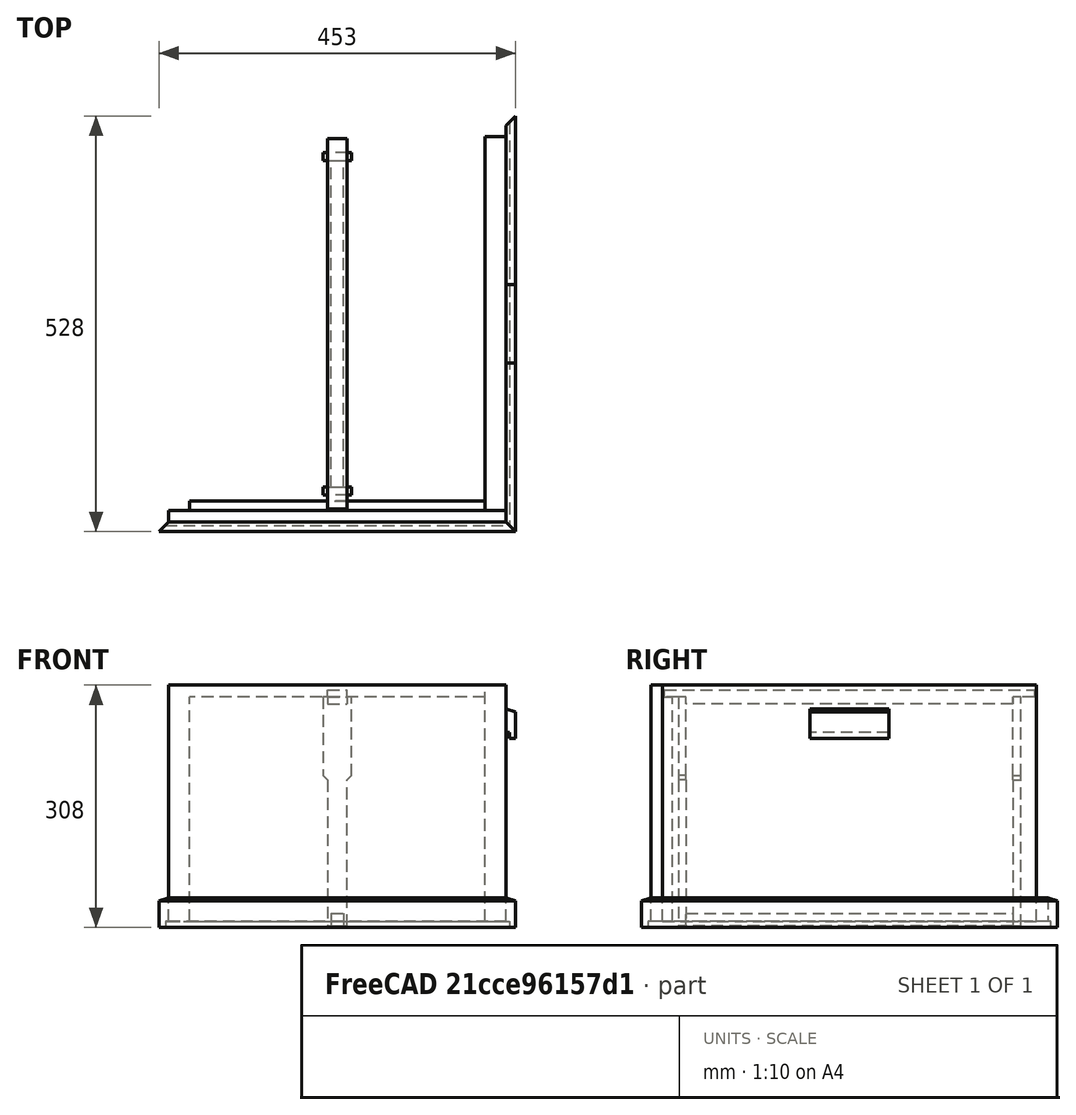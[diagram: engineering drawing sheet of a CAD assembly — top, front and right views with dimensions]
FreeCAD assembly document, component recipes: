
FREECAD ASSEMBLY — COMPONENT RECIPES ("naklada")

This assembly document has 6 components, labeled P0..P5 below (a component is one placed body or linked part). 6 of them carry a construction recipe — the FreeCAD feature program that regenerates the part from scratch, quoted from this document or its linked companion documents; the rest are supplied as boundary geometry only. No exploded tour is included for this assembly.
COMPONENT P0 — recipe-attached ("slat_side", modeled in this document).
Construction recipe (the document's own serialized feature program — sketch geometry with constraints, then the solid features built on it; lengths are millimeters unless a unit is written):

FEATURE [PartDesign::CoordinateSystem] LCS_0005
  AttacherType = Attacher::AttachEngine3D
  MapMode = 2
  Support = -> [X_Axis006]
FEATURE [Sketcher::SketchObject] Sketch003  label="Sketch004"
  FullyConstrained = true
  MapMode = 5
  Placement = pos=(0,0,0) rot=(1,0,0;1.5708rad)
  Support = -> [XZ_Plane006]
  expr: Constraints[12] = Variables.inner_width / 2 + Variables.wall_thickness
  sketch-geometry (6):
    g0: LineSegment StartX=214.5 StartY=0 StartZ=0 EndX=218.5 EndY=0 EndZ=0
    g1: LineSegment StartX=218.5 StartY=0 StartZ=0 EndX=218.5 EndY=-8 EndZ=0
    g2: LineSegment StartX=218.5 StartY=-8 StartZ=0 EndX=226.5 EndY=-8 EndZ=0
    g3: LineSegment StartX=226.5 StartY=-8 StartZ=0 EndX=226.5 EndY=25.6324 EndZ=0
    g4: LineSegment StartX=214.5 StartY=30 StartZ=0 EndX=214.5 EndY=0 EndZ=0
    g5: LineSegment StartX=214.5 StartY=30 StartZ=0 EndX=226.5 EndY=25.6324 EndZ=0
  constraints (18):
    c: Horizontal(g0)
    c: Coincident(g0,g1)
    c: Vertical(g1)
    c: Coincident(g1,g2)
    c: Horizontal(g2)
    c: Coincident(g2,g3)
    c: Vertical(g3)
    c: Coincident(g4,g0)
    c: Vertical(g4)
    c: DistanceX(g0,g0) = 4  'c'
    c: DistanceY(g1,g1) = 8  'd'
    c: Horizontal(g0,g-1)
    c: DistanceX(g-1,g0) = 214.5
    c: DistanceX(g0,g2) = 12  'a'
    c: DistanceY(g4,g4) = 30  'b'
    c: Coincident(g5,g4)
    c: Coincident(g5,g3)
    c: Angle(g5) = -0.349066  'e'
FEATURE [PartDesign::Pad] Pad002
  Direction = (1,1,1)
  Length = 700
  Length2 = 100
  Midplane = true
  Placement = pos=(0,0,0) rot=(1,0,0;1.5708rad)
  Profile = -> Sketch003
  Type = 0
FEATURE [Sketcher::SketchObject] Sketch004  label="Sketch005"
  ExternalGeometry = -> [Pad002]
  FullyConstrained = true
  MapMode = 5
  Support = -> [XY_Plane006]
  expr: Constraints[14] = Variables.inner_depth + 2 * Variables.wall_thickness
  sketch-geometry (8):
    g0: LineSegment StartX=226.5 StartY=-350 StartZ=0 EndX=226.5 EndY=-264 EndZ=0
    g1: LineSegment StartX=226.5 StartY=-264 StartZ=0 EndX=214.5 EndY=-252 EndZ=0
    g2: LineSegment StartX=214.5 StartY=-252 StartZ=0 EndX=214.5 EndY=-350 EndZ=0
    g3: LineSegment StartX=226.5 StartY=350 StartZ=0 EndX=226.5 EndY=264 EndZ=0
    g4: LineSegment StartX=226.5 StartY=264 StartZ=0 EndX=214.5 EndY=252 EndZ=0
    g5: LineSegment StartX=214.5 StartY=252 StartZ=0 EndX=214.5 EndY=350 EndZ=0
    g6: LineSegment StartX=214.5 StartY=-350 StartZ=0 EndX=226.5 EndY=-350 EndZ=0
    g7: LineSegment StartX=214.5 StartY=350 StartZ=0 EndX=226.5 EndY=350 EndZ=0
  constraints (20):
    c: Coincident(g0,g-4)
    c: Coincident(g1,g0)
    c: Coincident(g2,g1)
    c: Coincident(g2,g-4)
    c: Vertical(g2)
    c: Vertical(g0)
    c: Coincident(g-3,g3)
    c: Vertical(g3)
    c: Coincident(g3,g4)
    c: Coincident(g4,g5)
    c: Coincident(g5,g-3)
    c: Vertical(g5)
    c: Equal(g4,g1)
    c: Equal(g5,g2)
    c: DistanceY(g1,g4) = 504
    c: Coincident(g6,g2)
    c: Coincident(g6,g0)
    c: Coincident(g7,g5)
    c: Coincident(g7,g3)
    c: Perpendicular(g4,g1)
FEATURE [PartDesign::Pocket] Pocket001
  BaseFeature = -> Pad002
  Length = 41
  Length2 = 100
  Midplane = true
  Placement = pos=(0,0,0) rot=(1,0,0;1.5708rad)
  Profile = -> Sketch004
  Type = 1
FEATURE [PartDesign::Body] Body_3
  Group = -> [LCS_0005,Sketch003,Pad002,Sketch004,Pocket001]
  Origin = -> Origin006
  Tip = -> Pocket001
COMPONENT P1 — recipe-attached ("slat_front_rear", modeled in this document).
Construction recipe (the document's own serialized feature program — sketch geometry with constraints, then the solid features built on it; lengths are millimeters unless a unit is written):

FEATURE [PartDesign::CoordinateSystem] LCS_0007
  AttacherType = Attacher::AttachEngine3D
  MapMode = 2
  Support = -> [X_Axis008]
FEATURE [Sketcher::SketchObject] Sketch005  label="Sketch006"
  FullyConstrained = true
  MapMode = 5
  Placement = pos=(0,0,0) rot=(0.57735,0.57735,0.57735;2.0944rad)
  Support = -> [YZ_Plane008]
  expr: Constraints[17] = Variables.inner_depth / 2 + Variables.wall_thickness
  sketch-geometry (6):
    g0: LineSegment StartX=-252 StartY=0 StartZ=0 EndX=-252 EndY=30 EndZ=0
    g1: LineSegment StartX=-264 StartY=25.6324 StartZ=0 EndX=-264 EndY=-8 EndZ=0
    g2: LineSegment StartX=-264 StartY=-8 StartZ=0 EndX=-256 EndY=-8 EndZ=0
    g3: LineSegment StartX=-256 StartY=-8 StartZ=0 EndX=-256 EndY=0 EndZ=0
    g4: LineSegment StartX=-256 StartY=0 StartZ=0 EndX=-252 EndY=0 EndZ=0
    g5: LineSegment StartX=-264 StartY=25.6324 StartZ=0 EndX=-252 EndY=30 EndZ=0
  constraints (18):
    c: Vertical(g0)
    c: Vertical(g1)
    c: Coincident(g1,g2)
    c: Horizontal(g2)
    c: Coincident(g2,g3)
    c: Vertical(g3)
    c: Coincident(g3,g4)
    c: Coincident(g4,g0)
    c: Horizontal(g4)
    c: Horizontal(g0,g-1)
    c: DistanceX(g4,g4) = 4
    c: DistanceY(g3,g3) = 8
    c: DistanceX(g1,g0) = 12
    c: DistanceY(g0,g0) = 30
    c: Coincident(g5,g1)
    c: Coincident(g5,g0)
    c: Angle(g5) = 0.349066
    c: DistanceX(g0,g-1) = 252
FEATURE [PartDesign::Pad] Pad003
  Direction = (1,1,1)
  Length = 700
  Length2 = 100
  Midplane = true
  Placement = pos=(0,0,0) rot=(0.57735,0.57735,0.57735;2.0944rad)
  Profile = -> Sketch005
  Type = 0
FEATURE [Sketcher::SketchObject] Sketch006  label="Sketch007"
  ExternalGeometry = -> [Pad003]
  FullyConstrained = true
  MapMode = 5
  Support = -> [XY_Plane008]
  expr: Constraints[19] = Variables.inner_width + 2 * Variables.wall_thickness
  sketch-geometry (8):
    g0: LineSegment StartX=-350 StartY=-264 StartZ=0 EndX=-350 EndY=-252 EndZ=0
    g1: LineSegment StartX=-350 StartY=-252 StartZ=0 EndX=-214.5 EndY=-252 EndZ=0
    g2: LineSegment StartX=-214.5 StartY=-252 StartZ=0 EndX=-226.5 EndY=-264 EndZ=0
    g3: LineSegment StartX=-226.5 StartY=-264 StartZ=0 EndX=-350 EndY=-264 EndZ=0
    g4: LineSegment StartX=350 StartY=-264 StartZ=0 EndX=350 EndY=-252 EndZ=0
    g5: LineSegment StartX=350 StartY=-252 StartZ=0 EndX=214.5 EndY=-252 EndZ=0
    g6: LineSegment StartX=214.5 StartY=-252 StartZ=0 EndX=226.5 EndY=-264 EndZ=0
    g7: LineSegment StartX=226.5 StartY=-264 StartZ=0 EndX=350 EndY=-264 EndZ=0
  constraints (20):
    c: Coincident(g-3,g0)
    c: Coincident(g0,g-3)
    c: Coincident(g0,g1)
    c: Coincident(g1,g2)
    c: Coincident(g2,g3)
    c: Coincident(g3,g0)
    c: Coincident(g-4,g4)
    c: Coincident(g4,g-4)
    c: Coincident(g4,g5)
    c: Coincident(g5,g6)
    c: Coincident(g6,g7)
    c: Coincident(g7,g4)
    c: Perpendicular(g2,g6)
    c: Equal(g2,g6)
    c: Equal(g1,g5)
    c: Horizontal(g1)
    c: Horizontal(g3)
    c: Horizontal(g7)
    c: Horizontal(g5)
    c: DistanceX(g1,g5) = 429
FEATURE [PartDesign::Pocket] Pocket002
  BaseFeature = -> Pad003
  Length = 5
  Length2 = 100
  Midplane = true
  Placement = pos=(0,0,0) rot=(0.57735,0.57735,0.57735;2.0944rad)
  Profile = -> Sketch006
  Type = 1
FEATURE [PartDesign::Body] Body_4
  Group = -> [LCS_0007,Sketch005,Pad003,Sketch006,Pocket002]
  Origin = -> Origin008
  Tip = -> Pocket002
COMPONENT P2 — recipe-attached ("handle", modeled in this document).
Construction recipe (the document's own serialized feature program — sketch geometry with constraints, then the solid features built on it; lengths are millimeters unless a unit is written):

FEATURE [Sketcher::SketchObject] Sketch007  label="Sketch008"
  FullyConstrained = true
  MapMode = 5
  Placement = pos=(0,0,0) rot=(1,0,0;1.5708rad)
  Support = -> [XZ_Plane009]
  expr: Constraints[11] = Variables.inner_width / 2 + Variables.wall_thickness
  expr: Constraints[17] = Variables.height - 30
  sketch-geometry (6):
    g0: LineSegment StartX=214.5 StartY=240 StartZ=0 EndX=218.5 EndY=240 EndZ=0
    g1: LineSegment StartX=218.5 StartY=240 StartZ=0 EndX=218.5 EndY=232 EndZ=0
    g2: LineSegment StartX=218.5 StartY=232 StartZ=0 EndX=226.5 EndY=232 EndZ=0
    g3: LineSegment StartX=226.5 StartY=232 StartZ=0 EndX=226.5 EndY=265.632 EndZ=0
    g4: LineSegment StartX=214.5 StartY=270 StartZ=0 EndX=214.5 EndY=240 EndZ=0
    g5: LineSegment StartX=214.5 StartY=270 StartZ=0 EndX=226.5 EndY=265.632 EndZ=0
  constraints (18):
    c: Horizontal(g0)
    c: Coincident(g0,g1)
    c: Vertical(g1)
    c: Coincident(g1,g2)
    c: Horizontal(g2)
    c: Coincident(g2,g3)
    c: Vertical(g3)
    c: Coincident(g4,g0)
    c: Vertical(g4)
    c: DistanceX(g0,g0) = 4  'c'
    c: DistanceY(g1,g1) = 8  'd'
    c: DistanceX(g-1,g0) = 214.5
    c: DistanceX(g0,g2) = 12  'a'
    c: DistanceY(g4,g4) = 30  'b'
    c: Coincident(g5,g4)
    c: Coincident(g5,g3)
    c: Angle(g5) = -0.349066  'e'
    c: DistanceY(g-1,g4) = 270
FEATURE [PartDesign::CoordinateSystem] LCS_0008
  AttacherType = Attacher::AttachEngine3D
  MapMode = 2
  Support = -> [X_Axis010]
FEATURE [PartDesign::Pad] Pad004
  Direction = (1,1,1)
  Length = 100
  Length2 = 100
  Midplane = true
  Placement = pos=(0,0,0) rot=(1,0,0;1.5708rad)
  Profile = -> Sketch007
  Type = 0
FEATURE [PartDesign::Body] Body_005
  Group = -> [LCS_0008,Sketch007,Pad004]
  Origin = -> Origin009
  Tip = -> Pad004
COMPONENT P3 — recipe-attached ("wall_front_rear", modeled in this document).
Construction recipe (the document's own serialized feature program — sketch geometry with constraints, then the solid features built on it; lengths are millimeters unless a unit is written):

FEATURE [PartDesign::CoordinateSystem] LCS_0001
  AttacherType = Attacher::AttachEngine3D
  MapMode = 2
  Support = -> [X_Axis002]
FEATURE [Sketcher::SketchObject] Sketch  label="Sketch001"
  FullyConstrained = true
  MapMode = 5
  Support = -> [XY_Plane002]
  expr: Constraints[16] = Variables.inner_width
  expr: Constraints[17] = Variables.wall_thickness
  expr: Constraints[22] = Variables.inner_depth / 2
  expr: Constraints[19] = Variables.wall_thickness
  expr: Constraints[18] = Variables.wall_cut
  sketch-geometry (8):
    g0: LineSegment StartX=-187.5 StartY=-225 StartZ=0 EndX=187.5 EndY=-225 EndZ=0
    g1: LineSegment StartX=187.5 StartY=-225 StartZ=0 EndX=187.5 EndY=-237.5 EndZ=0
    g2: LineSegment StartX=187.5 StartY=-237.5 StartZ=0 EndX=214.5 EndY=-237.5 EndZ=0
    g3: LineSegment StartX=214.5 StartY=-237.5 StartZ=0 EndX=214.5 EndY=-252 EndZ=0
    g4: LineSegment StartX=214.5 StartY=-252 StartZ=0 EndX=-214.5 EndY=-252 EndZ=0
    g5: LineSegment StartX=-214.5 StartY=-252 StartZ=0 EndX=-214.5 EndY=-237.5 EndZ=0
    g6: LineSegment StartX=-214.5 StartY=-237.5 StartZ=0 EndX=-187.5 EndY=-237.5 EndZ=0
    g7: LineSegment StartX=-187.5 StartY=-237.5 StartZ=0 EndX=-187.5 EndY=-225 EndZ=0
  constraints (23):
    c: Coincident(g0,g1)
    c: Coincident(g1,g2)
    c: Horizontal(g2)
    c: Coincident(g2,g3)
    c: Vertical(g3)
    c: Coincident(g3,g4)
    c: Horizontal(g4)
    c: Coincident(g4,g5)
    c: Vertical(g5)
    c: Coincident(g5,g6)
    c: Horizontal(g6)
    c: Coincident(g6,g7)
    c: Vertical(g7)
    c: Vertical(g1)
    c: Horizontal(g6,g1)
    c: Equal(g6,g2)
    c: DistanceX(g0,g0) = 375
    c: DistanceX(g2,g2) = 27
    c: DistanceY(g1,g1) = 12.5
    c: DistanceY(g3,g0) = 27
    c: Coincident(g0,g7)
    c: Symmetric(g0,g0,g-2)
    c: DistanceY(g0,g-1) = 225
FEATURE [PartDesign::Pad] Pad
  Direction = (1,1,1)
  Length = 300
  Length2 = 100
  Profile = -> Sketch
  Type = 0
  expr: Length = Variables.height
FEATURE [Sketcher::SketchObject] Sketch001  label="Sketch002"
  ExternalGeometry = -> [Pad]
  FullyConstrained = true
  MapMode = 5
  Placement = pos=(0,0,0) rot=(0.57735,0.57735,0.57735;2.0944rad)
  Support = -> [YZ_Plane002]
  expr: Constraints[9] = Variables.frame_cut
  sketch-geometry (4):
    g0: LineSegment StartX=-225 StartY=300 StartZ=0 EndX=-237.5 EndY=300 EndZ=0
    g1: LineSegment StartX=-237.5 StartY=300 StartZ=0 EndX=-237.5 EndY=285 EndZ=0
    g2: LineSegment StartX=-237.5 StartY=285 StartZ=0 EndX=-225 EndY=285 EndZ=0
    g3: LineSegment StartX=-225 StartY=285 StartZ=0 EndX=-225 EndY=300 EndZ=0
  constraints (10):
    c: Coincident(g0,g1)
    c: Coincident(g1,g2)
    c: Coincident(g2,g3)
    c: Coincident(g3,g0)
    c: Horizontal(g2)
    c: Vertical(g1)
    c: Vertical(g3)
    c: Coincident(g0,g-3)
    c: Coincident(g0,g-3)
    c: DistanceY(g3,g3) = 15
FEATURE [PartDesign::Pocket] Pocket
  BaseFeature = -> Pad
  Length = 5
  Length2 = 100
  Midplane = true
  Profile = -> Sketch001
  Type = 1
FEATURE [PartDesign::Body] Body
  Group = -> [LCS_0001,Sketch,Pad,Sketch001,Pocket]
  Origin = -> Origin002
  Tip = -> Pocket
COMPONENT P4 — recipe-attached ("frame", modeled in this document).
Construction recipe (the document's own serialized feature program — sketch geometry with constraints, then the solid features built on it; lengths are millimeters unless a unit is written):

FEATURE [PartDesign::CoordinateSystem] LCS_0011
  AttacherType = Attacher::AttachEngine3D
  MapMode = 2
  Support = -> [X_Axis012]
FEATURE [Sketcher::SketchObject] Sketch008  label="Sketch009"
  FullyConstrained = true
  MapMode = 5
  Placement = pos=(0,0,0) rot=(0.57735,0.57735,0.57735;2.0944rad)
  Support = -> [YZ_Plane012]
  expr: Constraints[22] = Variables.height - Variables.frame_cut
  sketch-geometry (8):
    g0: LineSegment StartX=-235 StartY=294 StartZ=0 EndX=235 EndY=294 EndZ=0
    g1: LineSegment StartX=235 StartY=294 StartZ=0 EndX=235 EndY=285 EndZ=0
    g2: LineSegment StartX=235 StartY=285 StartZ=0 EndX=207.5 EndY=285 EndZ=0
    g3: LineSegment StartX=207.5 StartY=285 StartZ=0 EndX=207.5 EndY=276 EndZ=0
    g4: LineSegment StartX=207.5 StartY=276 StartZ=0 EndX=-207.5 EndY=276 EndZ=0
    g5: LineSegment StartX=-207.5 StartY=276 StartZ=0 EndX=-207.5 EndY=285 EndZ=0
    g6: LineSegment StartX=-207.5 StartY=285 StartZ=0 EndX=-235 EndY=285 EndZ=0
    g7: LineSegment StartX=-235 StartY=285 StartZ=0 EndX=-235 EndY=294 EndZ=0
  constraints (23):
    c: Horizontal(g0)
    c: Coincident(g0,g1)
    c: Vertical(g1)
    c: Coincident(g1,g2)
    c: Horizontal(g2)
    c: Coincident(g2,g3)
    c: Vertical(g3)
    c: Coincident(g3,g4)
    c: Horizontal(g4)
    c: Coincident(g4,g5)
    c: Vertical(g5)
    c: Coincident(g5,g6)
    c: Coincident(g6,g7)
    c: Coincident(g7,g0)
    c: Horizontal(g6)
    c: Vertical(g7)
    c: Symmetric(g5,g2,g-2)
    c: Equal(g6,g2)
    c: DistanceX(g0,g0) = 470
    c: DistanceX(g5,g2) = 415
    c: DistanceY(g1,g1) = 9
    c: DistanceY(g3,g0) = 18
    c: DistanceY(g-1,g6) = 285
FEATURE [PartDesign::Pad] Pad005
  Direction = (1,1,1)
  Length = 25
  Length2 = 100
  Midplane = true
  Placement = pos=(0,0,0) rot=(0.57735,0.57735,0.57735;2.0944rad)
  Profile = -> Sketch008
  Type = 0
FEATURE [Sketcher::SketchObject] Sketch010  label="Sketch011"
  ExternalGeometry = -> [Pad005]
  FullyConstrained = true
  MapMode = 5
  Placement = pos=(-9.13e-14,-207.5,4.57e-14) rot=(-0.57735,-0.57735,0.57735;4.18879rad)
  Support = -> [Pad005]
  expr: Constraints[21] = Variables.frame_height
  sketch-geometry (8):
    g0: LineSegment StartX=-285 StartY=18 StartZ=0 EndX=-285 EndY=-18 EndZ=0
    g1: LineSegment StartX=-285 StartY=-18 StartZ=0 EndX=-185 EndY=-18 EndZ=0
    g2: LineSegment StartX=-185 StartY=-18 StartZ=0 EndX=-179.5 EndY=-12.5 EndZ=0
    g3: LineSegment StartX=-179.5 StartY=-12.5 StartZ=0 EndX=6 EndY=-12.5 EndZ=0
    g4: LineSegment StartX=6 StartY=-12.5 StartZ=0 EndX=6 EndY=12.5 EndZ=0
    g5: LineSegment StartX=6 StartY=12.5 StartZ=0 EndX=-179.5 EndY=12.5 EndZ=0
    g6: LineSegment StartX=-179.5 StartY=12.5 StartZ=0 EndX=-185 EndY=18 EndZ=0
    g7: LineSegment StartX=-185 StartY=18 StartZ=0 EndX=-285 EndY=18 EndZ=0
  constraints (22):
    c: Coincident(g0,g1)
    c: Horizontal(g1)
    c: Coincident(g1,g2)
    c: Coincident(g2,g3)
    c: Horizontal(g3)
    c: Coincident(g3,g4)
    c: Coincident(g4,g5)
    c: Horizontal(g5)
    c: Coincident(g5,g6)
    c: Coincident(g6,g7)
    c: Coincident(g7,g0)
    c: Horizontal(g7)
    c: Vertical(g5,g2)
    c: Vertical(g1,g6)
    c: Symmetric(g0,g0,g-1)
    c: Symmetric(g4,g3,g-1)
    c: Perpendicular(g6,g2)
    c: DistanceY(g4,g4) = 25
    c: DistanceY(g0,g0) = 36
    c: DistanceX(g7,g7) = 100
    c: PointOnObject(g-3,g0)
    c: DistanceX(g-3,g4) = 300
FEATURE [PartDesign::Pad] Pad006
  BaseFeature = -> Pad005
  Direction = (1,1,1)
  Length = 10
  Length2 = 100
  Placement = pos=(0,0,0) rot=(0.57735,0.57735,0.57735;2.0944rad)
  Profile = -> Sketch010
  Type = 0
FEATURE [Sketcher::SketchObject] Sketch011  label="Sketch012"
  ExternalGeometry = -> [Pad006]
  FullyConstrained = true
  MapMode = 5
  Placement = pos=(9.13e-14,207.5,-4.57e-14) rot=(0.57735,0.57735,0.57735;4.18879rad)
  Support = -> [Pad006]
  sketch-geometry (8):
    g0: LineSegment StartX=-6 StartY=12.5 StartZ=0 EndX=179.5 EndY=12.5 EndZ=0
    g1: LineSegment StartX=179.5 StartY=12.5 StartZ=0 EndX=185 EndY=18 EndZ=0
    g2: LineSegment StartX=185 StartY=18 StartZ=0 EndX=285 EndY=18 EndZ=0
    g3: LineSegment StartX=285 StartY=18 StartZ=0 EndX=285 EndY=-18 EndZ=0
    g4: LineSegment StartX=285 StartY=-18 StartZ=0 EndX=185 EndY=-18 EndZ=0
    g5: LineSegment StartX=185 StartY=-18 StartZ=0 EndX=179.5 EndY=-12.5 EndZ=0
    g6: LineSegment StartX=179.5 StartY=-12.5 StartZ=0 EndX=-6 EndY=-12.5 EndZ=0
    g7: LineSegment StartX=-6 StartY=-12.5 StartZ=0 EndX=-6 EndY=12.5 EndZ=0
  constraints (17):
    c: Coincident(g-6,g0)
    c: Coincident(g0,g-3)
    c: Coincident(g0,g1)
    c: Coincident(g1,g-3)
    c: Coincident(g1,g2)
    c: Horizontal(g2)
    c: Coincident(g2,g3)
    c: Coincident(g3,g-5)
    c: Vertical(g3)
    c: Coincident(g3,g4)
    c: Coincident(g4,g-4)
    c: Coincident(g4,g5)
    c: Coincident(g5,g-4)
    c: Coincident(g5,g6)
    c: Coincident(g6,g-6)
    c: Coincident(g6,g7)
    c: Coincident(g7,g0)
FEATURE [PartDesign::Pad] Pad007
  BaseFeature = -> Pad006
  Direction = (1,1,1)
  Length = 10
  Length2 = 100
  Placement = pos=(0,0,0) rot=(0.57735,0.57735,0.57735;2.0944rad)
  Profile = -> Sketch011
  Type = 0
FEATURE [Sketcher::SketchObject] Sketch012  label="Sketch013"
  ExternalGeometry = -> [Pad007]
  FullyConstrained = true
  MapMode = 5
  Placement = pos=(0,0,0) rot=(0.57735,0.57735,0.57735;2.0944rad)
  Support = -> [YZ_Plane012]
  sketch-geometry (4):
    g0: LineSegment StartX=-207.5 StartY=10 StartZ=0 EndX=207.5 EndY=10 EndZ=0
    g1: LineSegment StartX=207.5 StartY=10 StartZ=0 EndX=207.5 EndY=-6 EndZ=0
    g2: LineSegment StartX=207.5 StartY=-6 StartZ=0 EndX=-207.5 EndY=-6 EndZ=0
    g3: LineSegment StartX=-207.5 StartY=-6 StartZ=0 EndX=-207.5 EndY=10 EndZ=0
  constraints (10):
    c: Coincident(g0,g1)
    c: Coincident(g1,g2)
    c: Coincident(g2,g3)
    c: Coincident(g3,g0)
    c: Horizontal(g0)
    c: Vertical(g1)
    c: Vertical(g3)
    c: Coincident(g1,g-4)
    c: Coincident(g2,g-3)
    c: DistanceY(g1,g1) = 16
FEATURE [PartDesign::Pad] Pad008
  BaseFeature = -> Pad007
  Direction = (1,1,1)
  Length = 16
  Length2 = 100
  Midplane = true
  Placement = pos=(0,0,0) rot=(0.57735,0.57735,0.57735;2.0944rad)
  Profile = -> Sketch012
  Type = 0
FEATURE [PartDesign::Body] Body_5
  Group = -> [LCS_0011,Sketch008,Pad005,Sketch010,Pad006,Sketch011,Pad007,Sketch012,Pad008]
  Origin = -> Origin012
  Tip = -> Pad008
COMPONENT P5 — recipe-attached ("wall_side", modeled in this document).
Construction recipe (the document's own serialized feature program — sketch geometry with constraints, then the solid features built on it; lengths are millimeters unless a unit is written):

FEATURE [PartDesign::CoordinateSystem] LCS_0003
  AttacherType = Attacher::AttachEngine3D
  MapMode = 2
  Support = -> [X_Axis004]
FEATURE [Sketcher::SketchObject] Sketch002  label="Sketch003"
  FullyConstrained = true
  MapMode = 5
  Support = -> [XY_Plane004]
  expr: Constraints[6] = Variables.wall_thickness
  expr: Constraints[7] = Variables.inner_depth + Variables.wall_cut * 2
  expr: Constraints[8] = Variables.inner_width / 2
  sketch-geometry (4):
    g0: LineSegment StartX=187.5 StartY=-237.5 StartZ=0 EndX=214.5 EndY=-237.5 EndZ=0
    g1: LineSegment StartX=214.5 StartY=-237.5 StartZ=0 EndX=214.5 EndY=237.5 EndZ=0
    g2: LineSegment StartX=214.5 StartY=237.5 StartZ=0 EndX=187.5 EndY=237.5 EndZ=0
    g3: LineSegment StartX=187.5 StartY=237.5 StartZ=0 EndX=187.5 EndY=-237.5 EndZ=0
  constraints (11):
    c: Coincident(g0,g1)
    c: Coincident(g1,g2)
    c: Coincident(g2,g3)
    c: Coincident(g3,g0)
    c: Horizontal(g0)
    c: Horizontal(g2)
    c: DistanceX(g0,g0) = 27
    c: DistanceY(g1,g1) = 475
    c: DistanceX(g-1,g0) = 187.5
    c: Vertical(g1)
    c: Symmetric(g0,g2,g-1)
FEATURE [PartDesign::Pad] Pad001
  Direction = (1,1,1)
  Length = 300
  Length2 = 100
  Profile = -> Sketch002
  Type = 0
  expr: Length = Variables.height
FEATURE [PartDesign::Body] Body_2
  Group = -> [LCS_0003,Sketch002,Pad001]
  Origin = -> Origin004
  Tip = -> Pad001
PROVENANCE & LICENSES
A FreeCAD (.FCStd) document from a public repository crawl; recipes are the document's own serialized feature recipes (and, for linked parts, companion documents' recipes).
License: apache-2.0.
